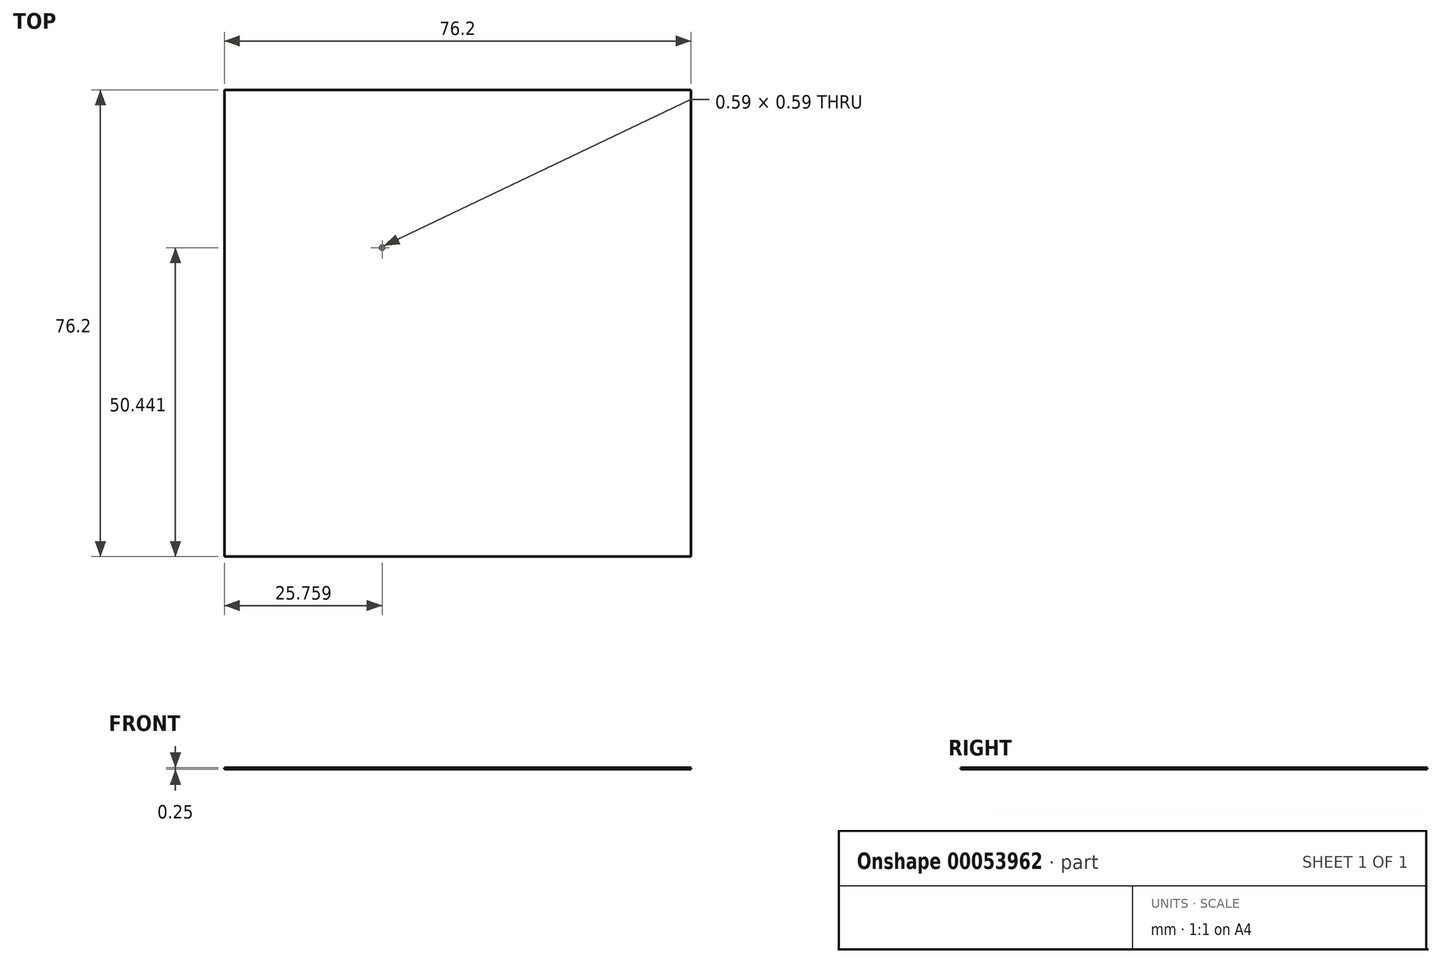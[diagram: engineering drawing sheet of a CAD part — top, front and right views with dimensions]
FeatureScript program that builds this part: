
annotation { "Feature Type Name" : "Feature", "Feature Type Description" : "" }
export const myFeature = defineFeature(function(context is Context, id is Id, definition is map)
    precondition{}
    {
        {
            var Q0;
            Q0=qCreatedBy(makeId("Top.planeOp"),FACE);
            var sketch = newSketch(context, id + "F0", { "sketchPlane" : qUnion([Q0])});
            skLineSegment(sketch, "E0.rect.bottom", {"start": v(-38.1, 38.1) * mm, "end": v(38.1, 38.1) * mm});
            skLineSegment(sketch, "E0.rect.top", {"start": v(-38.1, -38.1) * mm, "end": v(38.1, -38.1) * mm});
            skLineSegment(sketch, "E0.rect.left", {"start": v(-38.1, 38.1) * mm, "end": v(-38.1, -38.1) * mm});
            skLineSegment(sketch, "E0.rect.right", {"start": v(38.1, 38.1) * mm, "end": v(38.1, -38.1) * mm});
            skPoint(sketch, "E0.rect.middle", {"position": v(0, 0) * mm});
            skSolve(sketch);
        }
        {
            var Q0;
            Q0 = qSketchRegion(id + "F0", true);
            extrude(context, id + "F1", {"entities" : qUnion([Q0]), "depth" : 0.25 * mm});
        }
        {
            var Q0;
            Q0=makeQuery(id+"F1.opExtrude","CAP_FACE",FACE,{"disambiguationData":[OSD([sQuery(id+"F0.wireOp",EDGE,"E0.rect.bottom"),sQuery(id+"F0.wireOp",EDGE,"E0.rect.top"),sQuery(id+"F0.wireOp",EDGE,"E0.rect.left"),sQuery(id+"F0.wireOp",EDGE,"E0.rect.right")])],"isStart":false});
            var sketch = newSketch(context, id + "F2", { "sketchPlane" : qUnion([Q0])});
            skLineSegment(sketch, "E1.rect.bottom", {"start": v(-12.7, 12.7) * mm, "end": v(12.7, 12.7) * mm, "construction": true});
            skLineSegment(sketch, "E1.rect.top", {"start": v(-12.7, -12.7) * mm, "end": v(12.7, -12.7) * mm, "construction": true});
            skLineSegment(sketch, "E1.rect.left", {"start": v(-12.7, 12.7) * mm, "end": v(-12.7, -12.7) * mm, "construction": true});
            skLineSegment(sketch, "E1.rect.right", {"start": v(12.7, 12.7) * mm, "end": v(12.7, -12.7) * mm, "construction": true});
            skPoint(sketch, "E1.rect.middle", {"position": v(0, 0) * mm});
            skLineSegment(sketch, "E2.rect.bottom", {"start": v(-12.64, 12.64) * mm, "end": v(-12.04, 12.64) * mm});
            skLineSegment(sketch, "E2.rect.top", {"start": v(-12.64, 12.04) * mm, "end": v(-12.04, 12.04) * mm});
            skLineSegment(sketch, "E2.rect.left", {"start": v(-12.64, 12.64) * mm, "end": v(-12.64, 12.04) * mm});
            skLineSegment(sketch, "E2.rect.right", {"start": v(-12.04, 12.64) * mm, "end": v(-12.04, 12.04) * mm});
            skPoint(sketch, "E2.rect.middle", {"position": v(-12.34, 12.34) * mm});
            skSolve(sketch);
        }
        {
            var Q0;
            Q0 = qSketchRegion(id + "F2", true);
            extrude(context, id + "F3", {"entities" : qUnion([Q0]), "operationType" : NewBodyOperationType.REMOVE, "endBound" : BoundingType.THROUGH_ALL, "oppositeDirection" : true, "depth" : 25.4 * mm});
        }
    });
